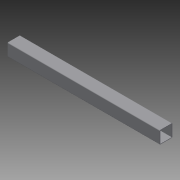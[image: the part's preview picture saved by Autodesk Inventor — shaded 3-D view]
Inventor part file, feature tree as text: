
AUTODESK INVENTOR PART (.ipt)
format: ipt  version: 2015 SP1 (Build 190203100, 203)  size: 84,992 bytes
history: native  units: in
note: dims shown in document units (in); Inventor stores cm internally (conversion verified against a paired STEP export)
features: extrude x1, fillet x1, sketch x1
ambient origin geometry x8: Origin, YZ Plane, XZ Plane, XY Plane, X Axis, Y Axis, Z Axis, Center Point
bodies: Solid1 (feature_tree)
feature tree (3):
  extrude  "Extrusion1"  Depth=2.0in
  fillet  "Fillet1"  Radius=0.083in
  sketch  "Sketch1"  dims[d0=2.0in d1=2.0in d2=0.083in d3=24.0in d4=0.0in d5=0.125in]
